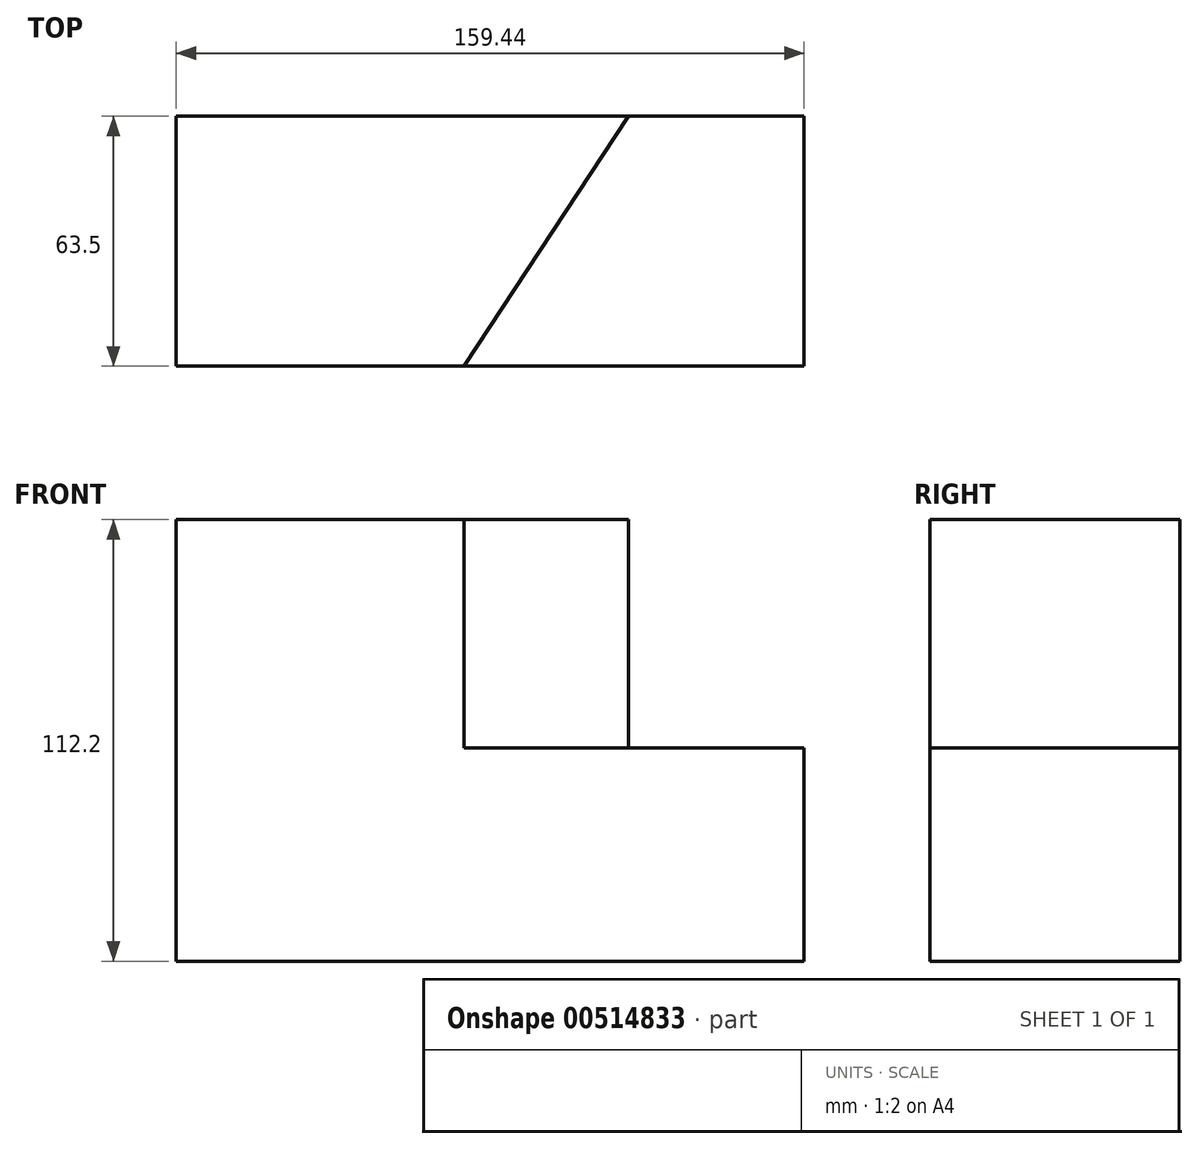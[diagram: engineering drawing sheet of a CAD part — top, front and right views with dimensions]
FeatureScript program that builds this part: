
annotation { "Feature Type Name" : "Feature", "Feature Type Description" : "" }
export const myFeature = defineFeature(function(context is Context, id is Id, definition is map)
    precondition{}
    {
        {
            var Q0;
            Q0=qCreatedBy(makeId("Front.planeOp"),FACE);
            var sketch = newSketch(context, id + "F0", { "sketchPlane" : qUnion([Q0])});
            skLineSegment(sketch, "E0.bottom", {"start": v(-66.72, 47.06) * mm, "end": v(92.72, 47.06) * mm});
            skLineSegment(sketch, "E0.top", {"start": v(-66.72, -71.76) * mm, "end": v(92.72, -71.76) * mm});
            skLineSegment(sketch, "E0.left", {"start": v(-66.72, 47.06) * mm, "end": v(-66.72, -71.76) * mm});
            skLineSegment(sketch, "E0.right", {"start": v(92.72, 47.06) * mm, "end": v(92.72, -71.76) * mm});
            skSolve(sketch);
        }
        {
            var Q0;
            Q0 = qSketchRegion(id + "F0", true);
            extrude(context, id + "F1", {"entities" : qUnion([Q0]), "depth" : 63.5 * mm, "offsetDistance" : 25.4 * mm});
        }
        {
            var Q0;
            Q0=makeQuery(id+"F1.opExtrude","CAP_FACE",FACE,{"disambiguationData":[OSD([sQuery(id+"F0.wireOp",EDGE,"E0.bottom"),sQuery(id+"F0.wireOp",EDGE,"E0.top"),sQuery(id+"F0.wireOp",EDGE,"E0.left"),sQuery(id+"F0.wireOp",EDGE,"E0.right")])],"isStart":false});
            var sketch = newSketch(context, id + "F2", { "sketchPlane" : qUnion([Q0])});
            skLineSegment(sketch, "E1.bottom", {"start": v(92.72, 47.06) * mm, "end": v(48.12, 47.06) * mm});
            skLineSegment(sketch, "E1.top", {"start": v(92.72, -17.54) * mm, "end": v(48.12, -17.54) * mm});
            skLineSegment(sketch, "E1.left", {"start": v(92.72, 47.06) * mm, "end": v(92.72, -17.54) * mm});
            skLineSegment(sketch, "E1.right", {"start": v(48.12, 47.06) * mm, "end": v(48.12, -17.54) * mm});
            skSolve(sketch);
        }
        {
            var Q0;
            Q0 = qSketchRegion(id + "F2", true);
            extrude(context, id + "F3", {"entities" : qUnion([Q0]), "operationType" : NewBodyOperationType.REMOVE, "oppositeDirection" : true, "depth" : 66.8 * mm, "offsetDistance" : 25.4 * mm});
        }
        {
            var Q0;
            Q0=makeQuery(id+"F1.opExtrude","SWEPT_FACE",FACE,{"disambiguationData":[OSD([sQuery(id+"F0.wireOp",EDGE,"E0.bottom")])]});
            var sketch = newSketch(context, id + "F4", { "sketchPlane" : qUnion([Q0])});
            skLineSegment(sketch, "E2", {"start": v(48.12, 0) * mm, "end": v(6.32, -63.5) * mm});
            skLineSegment(sketch, "E3", {"start": v(6.32, -63.5) * mm, "end": v(48.12, -63.5) * mm});
            skLineSegment(sketch, "E4", {"start": v(48.12, -63.5) * mm, "end": v(48.12, 0) * mm});
            skSolve(sketch);
        }
        {
            var Q0;
            Q0 = qSketchRegion(id + "F4", true);
            var Q1;
            Q1=makeQuery(id+"F3.boolean.opBoolean","COPY",FACE,{"derivedFrom":makeQuery(id+"F3.opExtrude","SWEPT_FACE",FACE,{"disambiguationData":[OSD([sQuery(id+"F2.wireOp",EDGE,"E1.top")])]})});
            extrude(context, id + "F5", {"entities" : qUnion([Q0]), "operationType" : NewBodyOperationType.REMOVE, "endBound" : BoundingType.UP_TO_SURFACE, "oppositeDirection" : true, "depth" : 64.52 * mm, "endBoundEntityFace" : qUnion([Q1]), "offsetDistance" : 25.4 * mm});
        }
        {
            var Q0;
            Q0=makeQuery(id+"F1.opExtrude","CAP_FACE",FACE,{"disambiguationData":[OSD([sQuery(id+"F0.wireOp",EDGE,"E0.bottom"),sQuery(id+"F0.wireOp",EDGE,"E0.top"),sQuery(id+"F0.wireOp",EDGE,"E0.left"),sQuery(id+"F0.wireOp",EDGE,"E0.right")])],"isStart":false});
            var sketch = newSketch(context, id + "F6", { "sketchPlane" : qUnion([Q0])});
            skLineSegment(sketch, "E5.bottom", {"start": v(-66.72, 47.06) * mm, "end": v(59.34, 47.06) * mm});
            skLineSegment(sketch, "E5.top", {"start": v(-66.72, 40.44) * mm, "end": v(59.34, 40.44) * mm});
            skLineSegment(sketch, "E5.left", {"start": v(-66.72, 47.06) * mm, "end": v(-66.72, 40.44) * mm});
            skLineSegment(sketch, "E5.right", {"start": v(59.34, 47.06) * mm, "end": v(59.34, 40.44) * mm});
            skSolve(sketch);
        }
        {
            var Q0;
            Q0 = qSketchRegion(id + "F6", true);
            extrude(context, id + "F7", {"entities" : qUnion([Q0]), "operationType" : NewBodyOperationType.REMOVE, "oppositeDirection" : true, "depth" : 70.87 * mm, "offsetDistance" : 25.4 * mm});
        }
    });
